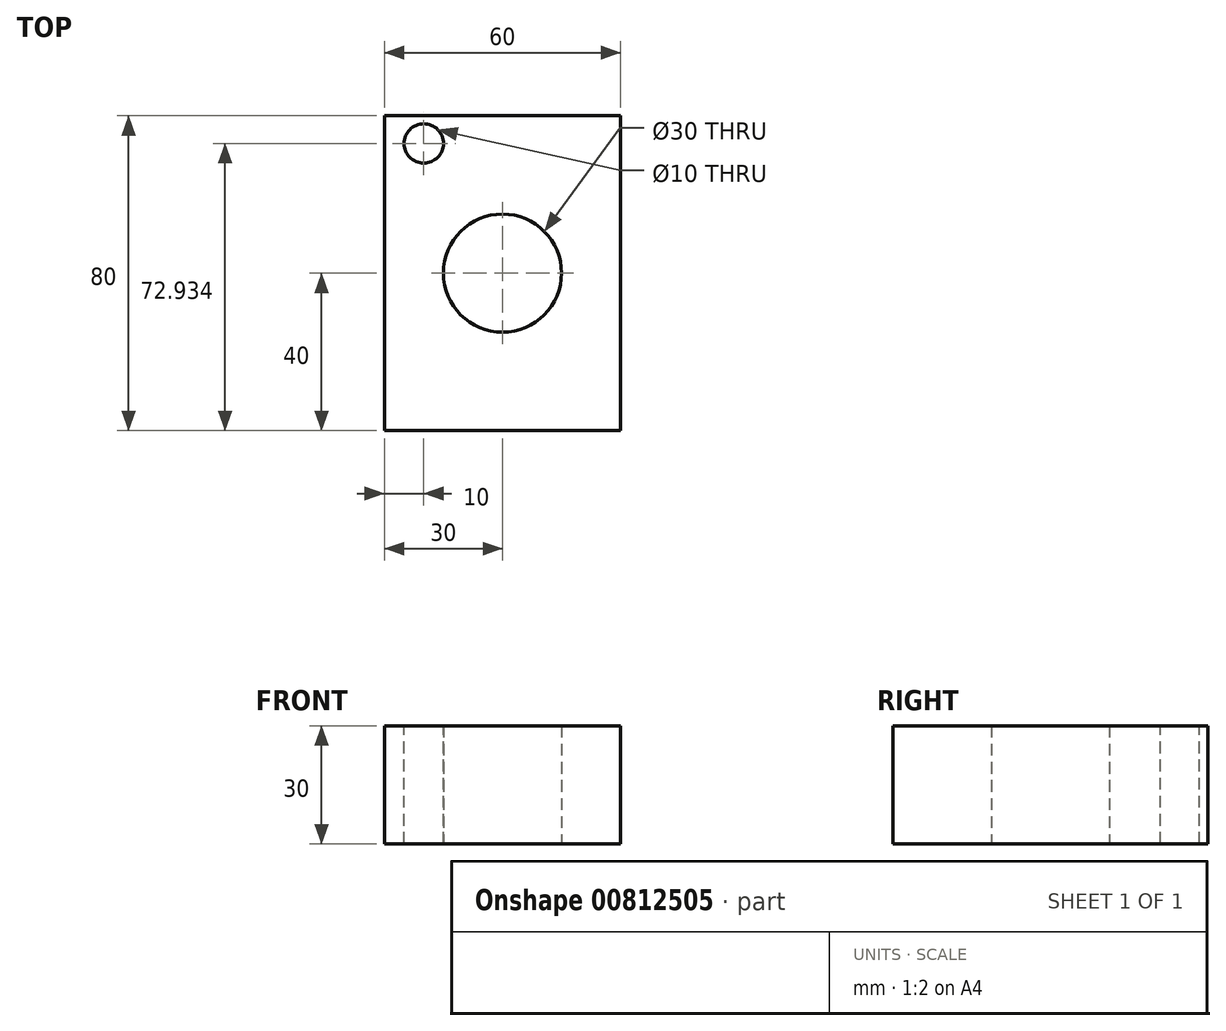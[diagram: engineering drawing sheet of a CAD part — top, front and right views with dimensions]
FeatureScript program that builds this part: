
annotation { "Feature Type Name" : "Feature", "Feature Type Description" : "" }
export const myFeature = defineFeature(function(context is Context, id is Id, definition is map)
    precondition{}
    {
        {
            var Q0;
            Q0=qCreatedBy(makeId("Top.planeOp"),FACE);
            var sketch = newSketch(context, id + "F0", { "sketchPlane" : qUnion([Q0])});
            skLineSegment(sketch, "E0.bottom", {"start": v(30, -40) * mm, "end": v(-30, -40) * mm});
            skLineSegment(sketch, "E0.top", {"start": v(30, 40) * mm, "end": v(-30, 40) * mm});
            skLineSegment(sketch, "E0.left", {"start": v(30, -40) * mm, "end": v(30, 40) * mm});
            skLineSegment(sketch, "E0.right", {"start": v(-30, -40) * mm, "end": v(-30, 40) * mm});
            skPoint(sketch, "E0.middle", {"position": v(0, 0) * mm});
            skCircle(sketch, "E1", {"center": v(0, 0) * mm, "radius": 15 * mm});
            skSolve(sketch);
        }
        {
            var Q0;
            Q0=makeQuery(id+"F0.imprint","IMPRINT",FACE,{"disambiguationData":[TD([[makeQuery(id+"F0.imprint","IMPRINT",EDGE,{"derivedFrom":sQuery(id+"F0.wireOp",EDGE,"E0.bottom")}),-1.0]])]});
            extrude(context, id + "F1", {"entities" : qUnion([Q0]), "depth" : 30 * mm, "offsetDistance" : 25.4 * mm});
        }
        {
            var Q0;
            Q0=qCreatedBy(makeId("Top.planeOp"),FACE);
            var sketch = newSketch(context, id + "F2", { "sketchPlane" : qUnion([Q0])});
            skCircle(sketch, "E2", {"center": v(-20, 32.93) * mm, "radius": 5 * mm});
            skSolve(sketch);
        }
        {
            var Q0;
            Q0 = qSketchRegion(id + "F2", true);
            extrude(context, id + "F3", {"entities" : qUnion([Q0]), "operationType" : NewBodyOperationType.REMOVE, "oppositeDirection" : true, "depth" : 25 * mm, "offsetDistance" : 25 * mm, "hasSecondDirection" : true, "secondDirectionOppositeDirection" : false, "secondDirectionDepth" : 44.5 * mm});
        }
    });
